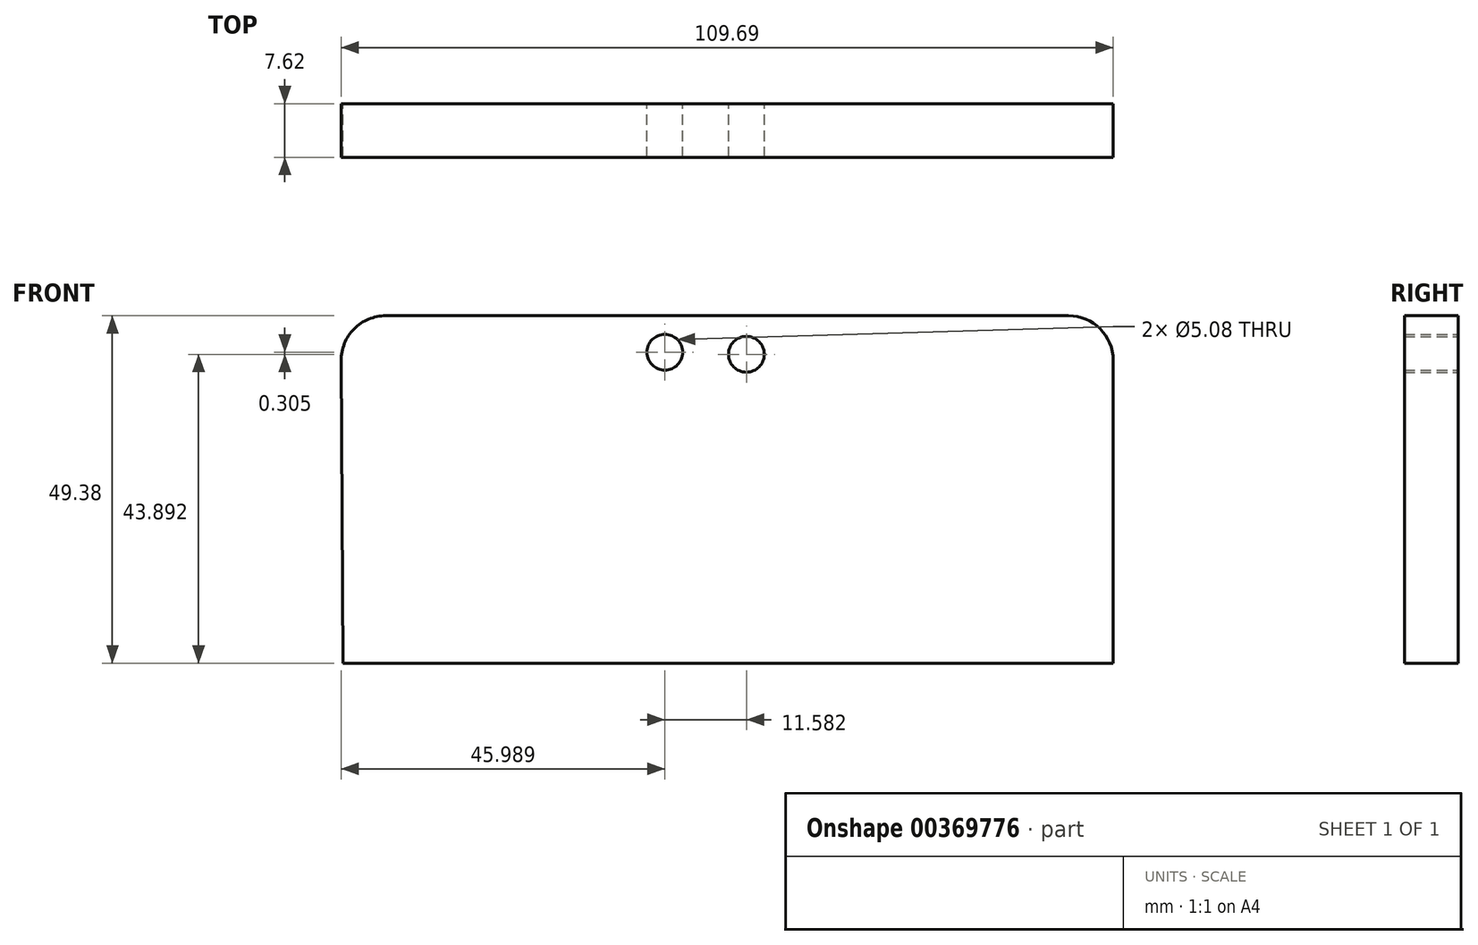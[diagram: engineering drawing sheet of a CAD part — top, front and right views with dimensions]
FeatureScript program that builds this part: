
annotation { "Feature Type Name" : "Feature", "Feature Type Description" : "" }
export const myFeature = defineFeature(function(context is Context, id is Id, definition is map)
    precondition{}
    {
        {
            var Q0;
            Q0=qCreatedBy(makeId("Front.planeOp"),FACE);
            var sketch = newSketch(context, id + "F0", { "sketchPlane" : qUnion([Q0])});
            skLineSegment(sketch, "E0", {"start": v(-46.04, 37.34) * mm, "end": v(50.95, 37.34) * mm});
            skLineSegment(sketch, "E1", {"start": v(57.3, 30.99) * mm, "end": v(57.3, -12.04) * mm});
            skLineSegment(sketch, "E2", {"start": v(57.3, -12.04) * mm, "end": v(-52.15, -12.04) * mm});
            skLineSegment(sketch, "E3", {"start": v(-52.15, -12.04) * mm, "end": v(-52.39, 30.95) * mm});
            skPoint(sketch, "E4.visualSharp", {"position": v(-52.43, 37.34) * mm});
            skArc(sketch, "E4.filletArc", {"start": v(-46.04, 37.34) * mm, "mid": v(-50.54, 35.47) * mm, "end": v(-52.39, 30.95) * mm});
            skPoint(sketch, "E5.visualSharp", {"position": v(57.3, 37.34) * mm});
            skArc(sketch, "E5.filletArc", {"start": v(57.3, 30.99) * mm, "mid": v(55.44, 35.48) * mm, "end": v(50.95, 37.34) * mm});
            skCircle(sketch, "E6", {"center": v(-6.4, 32.16) * mm, "radius": 2.54 * mm});
            skCircle(sketch, "E7", {"center": v(5.18, 31.85) * mm, "radius": 2.54 * mm});
            skLineSegment(sketch, "E8", {"start": v(55.83, -6.55) * mm, "end": v(55.83, -12.04) * mm});
            skLineSegment(sketch, "E9", {"start": v(55.83, -12.04) * mm, "end": v(54.56, -12.04) * mm});
            skLineSegment(sketch, "E10", {"start": v(54.56, -12.04) * mm, "end": v(54.56, -6.55) * mm});
            skLineSegment(sketch, "E11", {"start": v(54.56, -6.55) * mm, "end": v(55.83, -6.55) * mm});
            skLineSegment(sketch, "E12.MirrorCS", {"start": v(53.29, -6.55) * mm, "end": v(53.29, -12.04) * mm});
            skSolve(sketch);
        }
        {
            var Q0;
            Q0 = qSketchRegion(id + "F0", true);
            extrude(context, id + "F1", {"entities" : qUnion([Q0]), "depth" : 7.62 * mm});
        }
    });
